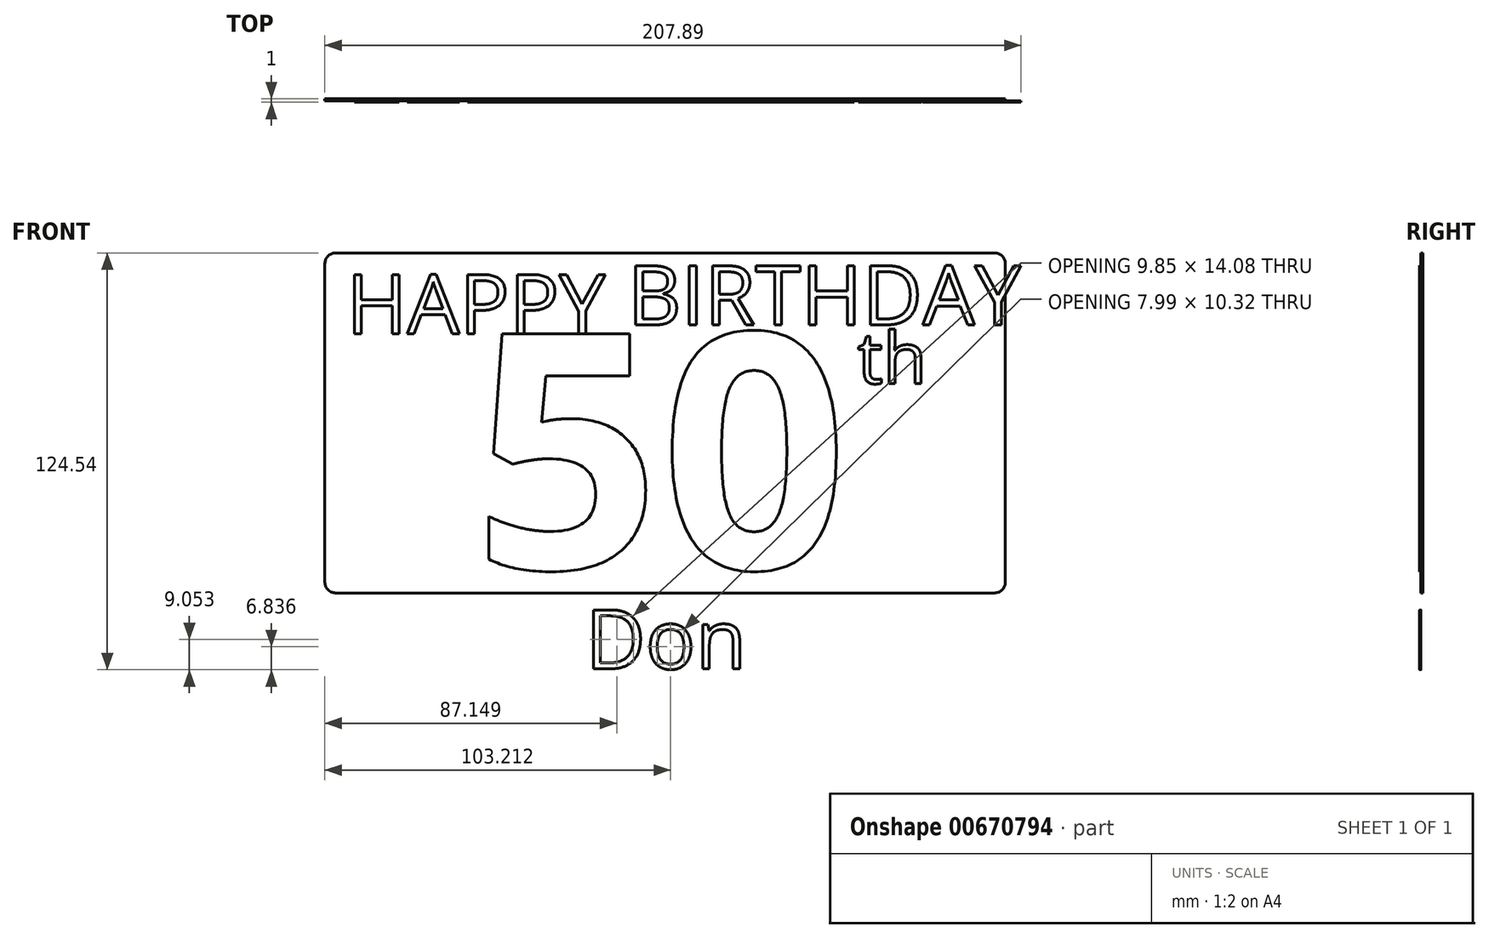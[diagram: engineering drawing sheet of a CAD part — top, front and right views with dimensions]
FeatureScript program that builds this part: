
annotation { "Feature Type Name" : "Feature", "Feature Type Description" : "" }
export const myFeature = defineFeature(function(context is Context, id is Id, definition is map)
    precondition{}
    {
        {
            var Q0;
            Q0=qCreatedBy(makeId("Front.planeOp"),FACE);
            var sketch = newSketch(context, id + "F0", { "sketchPlane" : qUnion([Q0])});
            skLineSegment(sketch, "E0.bottom", {"start": v(3.18, 0) * mm, "end": v(200.03, 0) * mm});
            skLineSegment(sketch, "E0.top", {"start": v(3.18, -101.6) * mm, "end": v(200.03, -101.6) * mm});
            skLineSegment(sketch, "E0.left", {"start": v(0, -3.17) * mm, "end": v(0, -98.43) * mm});
            skLineSegment(sketch, "E0.right", {"start": v(203.2, -3.17) * mm, "end": v(203.2, -98.43) * mm});
            skPoint(sketch, "E1.visualSharp", {"position": v(0, 0) * mm});
            skArc(sketch, "E1.filletArc", {"start": v(3.18, 0) * mm, "mid": v(0.93, -0.93) * mm, "end": v(0, -3.18) * mm});
            skPoint(sketch, "E2.visualSharp", {"position": v(203.2, 0) * mm});
            skArc(sketch, "E2.filletArc", {"start": v(203.2, -3.18) * mm, "mid": v(202.27, -0.93) * mm, "end": v(200.03, 0) * mm});
            skPoint(sketch, "E3.visualSharp", {"position": v(203.2, -101.6) * mm});
            skArc(sketch, "E3.filletArc", {"start": v(200.03, -101.6) * mm, "mid": v(202.27, -100.67) * mm, "end": v(203.2, -98.43) * mm});
            skPoint(sketch, "E4.visualSharp", {"position": v(0, -101.6) * mm});
            skArc(sketch, "E4.filletArc", {"start": v(0, -98.43) * mm, "mid": v(0.93, -100.67) * mm, "end": v(3.18, -101.6) * mm});
            skSolve(sketch);
        }
        {
            var Q0;
            Q0=qSketchRegion(id+"F0",true);
            extrude(context, id + "F1", {"entities" : qUnion([Q0]), "depth" : .6 * mm, "offsetDistance" : 25.4 * mm});
        }
        {
            var Q0;
            Q0=makeQuery(id+"F1.opExtrude","CAP_FACE",FACE,{"disambiguationData":[OSD([sQuery(id+"F0.wireOp",EDGE,"E0.bottom"),sQuery(id+"F0.wireOp",EDGE,"E0.top"),sQuery(id+"F0.wireOp",EDGE,"E0.left"),sQuery(id+"F0.wireOp",EDGE,"E0.right"),sQuery(id+"F0.wireOp",EDGE,"E1.filletArc"),sQuery(id+"F0.wireOp",EDGE,"E2.filletArc"),sQuery(id+"F0.wireOp",EDGE,"E3.filletArc"),sQuery(id+"F0.wireOp",EDGE,"E4.filletArc")])],"isStart":false});
            var sketch = newSketch(context, id + "F2", { "sketchPlane" : qUnion([Q0])});
            skText(sketch, "E5", { "text": "HAPPY", "fontName": "OpenSans-Regular.ttf"});
            skText(sketch, "E6", { "text": "BIRTHDAY", "fontName": "OpenSans-Regular.ttf"});
            skText(sketch, "E7", { "text": "50", "fontName": "OpenSans-Bold.ttf"});
            skText(sketch, "E8", { "text": "th", "fontName": "OpenSans-Regular.ttf"});
            skText(sketch, "E9", { "text": "Don", "fontName": "OpenSans-Regular.ttf"});
            const initialGuessF2  = {"E5": [0.00635, -0.02413, 1, 0, 0.01778], "E6": [0.0904, -0.0215, 1, 0, 0.01778], "E7": [0.04414, -0.09431, 1, 0, 0.07067], "E8": [0.15906, -0.03904, 1, 0, 0.0154], "E9": [0.07775, -0.1243, 1, 0, 0.01778]};
            skSetInitialGuess(sketch, initialGuessF2);
            skSolve(sketch);
        }
        {
            var Q0;
            Q0=qSketchRegion(id+"F2",true);
            extrude(context, id + "F3", {"entities" : qUnion([Q0]), "operationType" : NewBodyOperationType.ADD, "depth" : .4 * mm, "offsetDistance" : 25.4 * mm});
        }
    });
